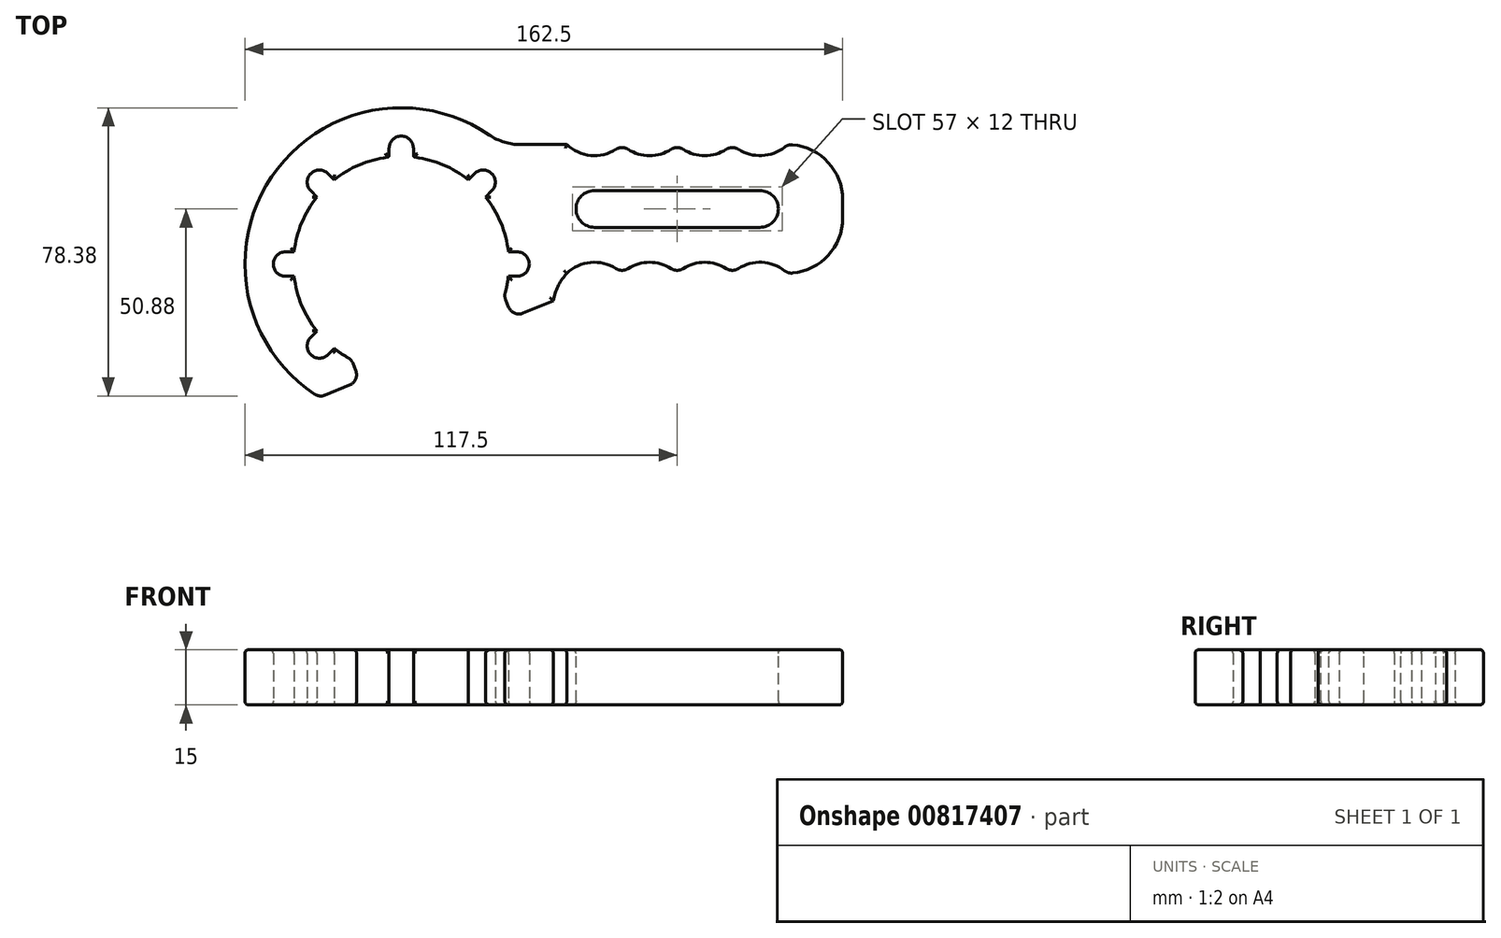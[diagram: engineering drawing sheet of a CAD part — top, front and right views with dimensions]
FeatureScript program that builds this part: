
annotation { "Feature Type Name" : "Feature", "Feature Type Description" : "" }
export const myFeature = defineFeature(function(context is Context, id is Id, definition is map)
    precondition{}
    {
        {
            var Q0;
            Q0=qCreatedBy(makeId("Top.planeOp"),FACE);
            var sketch = newSketch(context, id + "F0", { "sketchPlane" : qUnion([Q0])});
            skCircle(sketch, "E0", {"center": v(0, 0) * mm, "radius": 34.5 * mm});
            skLineSegment(sketch, "E1", {"start": v(0, 0) * mm, "end": v(0, 31.48) * mm, "construction": true});
            skLineSegment(sketch, "E2.bottom", {"start": v(-3.02, 0) * mm, "end": v(3.02, 0) * mm});
            skLineSegment(sketch, "E2.left", {"start": v(-3.02, 0) * mm, "end": v(-3.02, 34.37) * mm});
            skLineSegment(sketch, "E2.right", {"start": v(3.02, 0) * mm, "end": v(3.02, 34.37) * mm});
            skCircle(sketch, "E3", {"center": v(0, 0) * mm, "radius": 29 * mm});
            skCircle(sketch, "E4", {"center": v(0, 0) * mm, "radius": 12.5 * mm});
            skCircle(sketch, "E5", {"center": v(0, 31.48) * mm, "radius": 3.02 * mm});
            skPoint(sketch, "E5.first.point", {"position": v(0, 34.5) * mm});
            skPoint(sketch, "E5.second.point", {"position": v(-3.02, 31.48) * mm});
            skPoint(sketch, "E5.third.point", {"position": v(3.02, 31.48) * mm});
            skSolve(sketch);
        }
        {
            var Q0;
            {var subQ0=sQuery(id+"F0.wireOp",EDGE,"E5");var subQ2=sQuery(id+"F0.wireOp",EDGE,"E3");var subQ6=makeQuery(id+"F0.imprint","INTERSECT",VERTEX,{"disambiguationData":[OD(0.0)],"derivedFrom":[subQ2,subQ0]});Q0=makeQuery(id+"F0.imprint","IMPRINT",FACE,{"disambiguationData":[TD([[makeQuery(id+"F0.imprint","IMPRINT",EDGE,{"disambiguationData":[TD([[subQ6,-1.0]])],"derivedFrom":subQ2}),-1.0]])]});}
            var Q1;
            {var subQ0=sQuery(id+"F0.wireOp",EDGE,"E3");var subQ1=sQuery(id+"F0.wireOp",EDGE,"E2.left");var subQ2=makeQuery(id+"F0.imprint","INTERSECT",VERTEX,{"derivedFrom":[subQ1,subQ0]});Q1=makeQuery(id+"F0.imprint","IMPRINT",FACE,{"disambiguationData":[TD([[makeQuery(id+"F0.imprint","IMPRINT",EDGE,{"disambiguationData":[TD([[subQ2,-1.0]])],"derivedFrom":subQ1}),-1.0]])]});}
            var Q2;
            {var subQ0=sQuery(id+"F0.wireOp",EDGE,"E5");var subQ1=sQuery(id+"F0.wireOp",EDGE,"E3");var subQ2=makeQuery(id+"F0.imprint","INTERSECT",VERTEX,{"disambiguationData":[OD(0.0)],"derivedFrom":[subQ1,subQ0]});Q2=makeQuery(id+"F0.imprint","IMPRINT",FACE,{"disambiguationData":[TD([[makeQuery(id+"F0.imprint","IMPRINT",EDGE,{"disambiguationData":[TD([[subQ2,-1.0]])],"derivedFrom":subQ1}),1.0]])]});}
            var Q3;
            {var subQ0=sQuery(id+"F0.wireOp",EDGE,"E3");var subQ1=sQuery(id+"F0.wireOp",EDGE,"E2.right");var subQ2=makeQuery(id+"F0.imprint","INTERSECT",VERTEX,{"derivedFrom":[subQ1,subQ0]});Q3=makeQuery(id+"F0.imprint","IMPRINT",FACE,{"disambiguationData":[TD([[makeQuery(id+"F0.imprint","IMPRINT",EDGE,{"disambiguationData":[TD([[subQ2,-1.0]])],"derivedFrom":subQ1}),1.0]])]});}
            var Q4;
            {var subQ5=sQuery(id+"F0.wireOp",EDGE,"E2.left");var subQ8=sQuery(id+"F0.wireOp",EDGE,"E4");var subQ10=makeQuery(id+"F0.imprint","INTERSECT",VERTEX,{"derivedFrom":[subQ5,subQ8]});Q4=makeQuery(id+"F0.imprint","IMPRINT",FACE,{"disambiguationData":[TD([[makeQuery(id+"F0.imprint","IMPRINT",EDGE,{"disambiguationData":[TD([[subQ10,-1.0]])],"derivedFrom":subQ5}),-1.0]])]});}
            var Q5;
            {var subQ0=sQuery(id+"F0.wireOp",EDGE,"E2.bottom");Q5=makeQuery(id+"F0.imprint","IMPRINT",FACE,{"disambiguationData":[TD([[makeQuery(id+"F0.imprint","IMPRINT",EDGE,{"derivedFrom":subQ0}),-1.0]])]});}
            var Q6;
            {var subQ0=sQuery(id+"F0.wireOp",EDGE,"E2.bottom");Q6=makeQuery(id+"F0.imprint","IMPRINT",FACE,{"disambiguationData":[TD([[makeQuery(id+"F0.imprint","IMPRINT",EDGE,{"derivedFrom":subQ0}),1.0]])]});}
            var Q7;
            {var subQ0=sQuery(id+"F0.wireOp",EDGE,"E4");var subQ1=sQuery(id+"F0.wireOp",EDGE,"E2.left");var subQ2=makeQuery(id+"F0.imprint","INTERSECT",VERTEX,{"derivedFrom":[subQ1,subQ0]});Q7=makeQuery(id+"F0.imprint","IMPRINT",FACE,{"disambiguationData":[TD([[makeQuery(id+"F0.imprint","IMPRINT",EDGE,{"disambiguationData":[TD([[subQ2,-1.0]])],"derivedFrom":subQ1}),1.0]])]});}
            extrude(context, id + "F1", {"entities" : qUnion([Q0, Q1, Q2, Q3, Q4, Q5, Q6, Q7]), "depth" : 30 * mm, "offsetDistance" : 25 * mm});
        }
        {
            var Q0;
            Q0=makeQuery(id+"F1.opExtrude","SWEPT_BODY",BODY,{"disambiguationData":[OSD([sQuery(id+"F0.wireOp",EDGE,"E0"),sQuery(id+"F0.wireOp",EDGE,"E2.left"),sQuery(id+"F0.wireOp",EDGE,"E2.right"),sQuery(id+"F0.wireOp",EDGE,"E3"),sQuery(id+"F0.wireOp",EDGE,"E4")])]});
            var Q1;
            Q1=makeQuery(id+"F1.opExtrude","SWEPT_FACE",FACE,{"disambiguationData":[OSD([sQuery(id+"F0.wireOp",EDGE,"E3")])]});
            circularPattern(context, id + "F2", {"operationType" : NewBodyOperationType.ADD, "entities" : qUnion([Q0]), "axis" : qUnion([Q1]), "angle" : 360 * degree, "instanceCount" : 8, "equalSpace" : true});
        }
        {
            var Q0;
            {var subQ0=makeQuery(id+"F1.opExtrude","CAP_FACE",FACE,{"disambiguationData":[OSD([sQuery(id+"F0.wireOp",EDGE,"E0"),sQuery(id+"F0.wireOp",EDGE,"E2.left"),sQuery(id+"F0.wireOp",EDGE,"E2.right"),sQuery(id+"F0.wireOp",EDGE,"E3"),sQuery(id+"F0.wireOp",EDGE,"E4")])],"isStart":false});Q0=makeQuery(id+"F2.boolean.opBoolean","MERGE",FACE,{"derivedFrom":[subQ0,makeQuery(id+"F2.opPattern","COPY",FACE,{"derivedFrom":subQ0,"instanceName":"1"}),makeQuery(id+"F2.opPattern","COPY",FACE,{"derivedFrom":subQ0,"instanceName":"2"}),makeQuery(id+"F2.opPattern","COPY",FACE,{"derivedFrom":subQ0,"instanceName":"3"}),makeQuery(id+"F2.opPattern","COPY",FACE,{"derivedFrom":subQ0,"instanceName":"4"}),makeQuery(id+"F2.opPattern","COPY",FACE,{"derivedFrom":subQ0,"instanceName":"5"})]});}
            var sketch = newSketch(context, id + "F3", { "sketchPlane" : qUnion([Q0])});
            skCircle(sketch, "E6", {"center": v(0, 0) * mm, "radius": 42.5 * mm});
            skCircle(sketch, "E7", {"center": v(0, 0) * mm, "radius": 22.5 * mm});
            skLineSegment(sketch, "E8.bottom", {"start": v(0, 32.5) * mm, "end": v(120, 32.5) * mm});
            skLineSegment(sketch, "E8.top", {"start": v(0, -2.5) * mm, "end": v(120, -2.5) * mm});
            skLineSegment(sketch, "E8.left", {"start": v(0, 42.5) * mm, "end": v(0, -2.5) * mm});
            skLineSegment(sketch, "E8.right", {"start": v(120, 32.5) * mm, "end": v(120, -2.5) * mm});
            skLineSegment(sketch, "E9", {"start": v(0, 0) * mm, "end": v(25.3, -61.06) * mm, "construction": true});
            skLineSegment(sketch, "E10", {"start": v(20.79, 8.61) * mm, "end": v(46.08, -52.45) * mm});
            skLineSegment(sketch, "E11", {"start": v(46.08, -52.45) * mm, "end": v(4.5, -69.67) * mm});
            skLineSegment(sketch, "E12", {"start": v(4.5, -69.67) * mm, "end": v(-20.79, -8.61) * mm});
            skLineSegment(sketch, "E13", {"start": v(-20.79, -8.61) * mm, "end": v(20.79, 8.61) * mm});
            skLineSegment(sketch, "E14", {"start": v(-22.19, -36.25) * mm, "end": v(41.32, -9.94) * mm});
            skSolve(sketch);
        }
        {
            var Q0;
            {var subQ5=sQuery(id+"F3.wireOp",EDGE,"E8.right");Q0=makeQuery(id+"F3.imprint","IMPRINT",FACE,{"disambiguationData":[TD([[makeQuery(id+"F3.imprint","IMPRINT",EDGE,{"derivedFrom":subQ5}),-1.0]])]});}
            var Q1;
            {var subQ4=sQuery(id+"F0.wireOp",EDGE,"E2.right");var subQ5=makeQuery(id+"F1.opExtrude","CAP_EDGE",EDGE,{"disambiguationData":[OSD([subQ4])],"isStart":false});Q1=makeQuery(id+"F3.imprint","IMPRINT",FACE,{"disambiguationData":[TD([[makeQuery(id+"F3.imprint","IMPRINT",EDGE,{"derivedFrom":subQ5}),-1.0]])]});}
            var Q2;
            {var subQ3=sQuery(id+"F3.wireOp",EDGE,"E8.left");var subQ5=sQuery(id+"F3.wireOp",EDGE,"E6");var subQ6=makeQuery(id+"F3.imprint","INTERSECT",VERTEX,{"derivedFrom":[subQ5,subQ3]});Q2=makeQuery(id+"F3.imprint","IMPRINT",FACE,{"disambiguationData":[TD([[makeQuery(id+"F3.imprint","IMPRINT",EDGE,{"disambiguationData":[TD([[subQ6,1.0]])],"derivedFrom":subQ5}),1.0]])]});}
            var Q3;
            {var subQ2=sQuery(id+"F0.wireOp",EDGE,"E2.left");var subQ25=makeQuery(id+"F1.opExtrude","CAP_EDGE",EDGE,{"disambiguationData":[OSD([subQ2])],"isStart":false});Q3=makeQuery(id+"F3.imprint","IMPRINT",FACE,{"disambiguationData":[TD([[makeQuery(id+"F3.imprint","IMPRINT",EDGE,{"derivedFrom":subQ25}),1.0]])]});}
            var Q4;
            {var subQ5=sQuery(id+"F0.wireOp",EDGE,"E2.right");var subQ16=makeQuery(id+"F2.opPattern","COPY",EDGE,{"derivedFrom":makeQuery(id+"F1.opExtrude","CAP_EDGE",EDGE,{"disambiguationData":[OSD([subQ5])],"isStart":false}),"instanceName":"6"});Q4=makeQuery(id+"F3.imprint","IMPRINT",FACE,{"disambiguationData":[TD([[makeQuery(id+"F3.imprint","IMPRINT",EDGE,{"derivedFrom":subQ16}),-1.0]])]});}
            var Q5;
            {var subQ7=sQuery(id+"F0.wireOp",EDGE,"E2.right");var subQ8=makeQuery(id+"F2.opPattern","COPY",EDGE,{"derivedFrom":makeQuery(id+"F1.opExtrude","CAP_EDGE",EDGE,{"disambiguationData":[OSD([subQ7])],"isStart":false}),"instanceName":"2"});Q5=makeQuery(id+"F3.imprint","IMPRINT",FACE,{"disambiguationData":[TD([[makeQuery(id+"F3.imprint","IMPRINT",EDGE,{"derivedFrom":subQ8}),-1.0]])]});}
            var Q6;
            {var subQ0=makeQuery(id+"F1.opExtrude","CAP_FACE",FACE,{"disambiguationData":[OSD([sQuery(id+"F0.wireOp",EDGE,"E0"),sQuery(id+"F0.wireOp",EDGE,"E2.left"),sQuery(id+"F0.wireOp",EDGE,"E2.right"),sQuery(id+"F0.wireOp",EDGE,"E3"),sQuery(id+"F0.wireOp",EDGE,"E4")])],"isStart":false});Q6=makeQuery(id+"F2.boolean.opBoolean","MERGE",FACE,{"derivedFrom":[subQ0,makeQuery(id+"FdRA7V0R3QqqVRS_1.opRevolve","SWEPT_FACE",FACE,{"disambiguationData":[OSD([sQuery(id+"FKEeH5BDUjIDk6X_1.wireOp",EDGE,"wVb3vfNX-KfGu-E7eh-lrTJ-hg433LaZDyXz")])]}),makeQuery(id+"F2.opPattern","COPY",FACE,{"derivedFrom":subQ0,"instanceName":"1"}),makeQuery(id+"F2.opPattern","COPY",FACE,{"derivedFrom":subQ0,"instanceName":"2"}),makeQuery(id+"F2.opPattern","COPY",FACE,{"derivedFrom":subQ0,"instanceName":"3"}),makeQuery(id+"F2.opPattern","COPY",FACE,{"derivedFrom":subQ0,"instanceName":"4"}),makeQuery(id+"F2.opPattern","COPY",FACE,{"derivedFrom":subQ0,"instanceName":"5"})]});}
            extrude(context, id + "F4", {"entities" : qUnion([Q0, Q1, Q2, Q3, Q4, Q5]), "oppositeDirection" : true, "depth" : 15 * mm, "endBoundEntityFace" : qUnion([Q6]), "offsetDistance" : 25 * mm});
        }
        {
            var Q0;
            Q0=makeQuery(id+"F1.opExtrude","SWEPT_BODY",BODY,{"disambiguationData":[OSD([sQuery(id+"F0.wireOp",EDGE,"E0"),sQuery(id+"F0.wireOp",EDGE,"E2.left"),sQuery(id+"F0.wireOp",EDGE,"E2.right"),sQuery(id+"F0.wireOp",EDGE,"E3"),sQuery(id+"F0.wireOp",EDGE,"E4")])]});
            var Q1;
            Q1=makeQuery(id+"F4.opExtrude","SWEPT_BODY",BODY,{"disambiguationData":[OSD([sQuery(id+"F3.wireOp",EDGE,"E6")])]});
            booleanBodies(context, id + "F5", {"operationType" : BooleanOperationType.SUBTRACTION, "tools" : qUnion([Q0]), "targets" : qUnion([Q1]), "offset" : true, "offsetAll" : true, "offsetDistance" : .3 * mm});
        }
        {
            var Q0;
            Q0=makeQuery(id+"F4.opExtrude","CAP_FACE",FACE,{"disambiguationData":[OSD([sQuery(id+"F0.wireOp",EDGE,"E0"),sQuery(id+"F0.wireOp",EDGE,"E2.left"),sQuery(id+"F0.wireOp",EDGE,"E2.right"),sQuery(id+"F0.wireOp",EDGE,"E3"),sQuery(id+"F0.wireOp",EDGE,"68155f5a-aa5a-4abc-ae5a-2b9c3076ed17"),sQuery(id+"F0.wireOp",EDGE,"543f8d36-851c-4509-9e67-5f2352c07657"),sQuery(id+"F3.wireOp",EDGE,"E6"),sQuery(id+"F3.wireOp",EDGE,"E8.bottom"),sQuery(id+"F3.wireOp",EDGE,"E8.top"),sQuery(id+"F3.wireOp",EDGE,"E8.right"),sQuery(id+"F3.wireOp",EDGE,"E10"),sQuery(id+"F3.wireOp",EDGE,"E12"),sQuery(id+"F3.wireOp",EDGE,"E14")])],"isStart":true});
            var sketch = newSketch(context, id + "F6", { "sketchPlane" : qUnion([Q0])});
            skCircle(sketch, "E15", {"center": v(97.5, 40.37) * mm, "radius": 10.87 * mm});
            skCircle(sketch, "E16", {"center": v(97.5, -10.38) * mm, "radius": 10.87 * mm});
            skPoint(sketch, "E17", {"position": v(97.5, 29.5) * mm});
            skPoint(sketch, "E18", {"position": v(97.5, 0.5) * mm});
            skLineSegment(sketch, "E19", {"start": v(120, 15) * mm, "end": v(33.65, 15) * mm, "construction": true});
            skPoint(sketch, "E20", {"position": v(90, 32.5) * mm});
            skPoint(sketch, "E21", {"position": v(105, 32.5) * mm});
            skCircle(sketch, "E22.1.0.0", {"center": v(82.5, 40.37) * mm, "radius": 10.87 * mm});
            skCircle(sketch, "E22.1.0.1", {"center": v(82.5, -10.38) * mm, "radius": 10.87 * mm});
            skCircle(sketch, "E22.2.0.0", {"center": v(67.5, 40.37) * mm, "radius": 10.87 * mm});
            skCircle(sketch, "E22.2.0.1", {"center": v(67.5, -10.38) * mm, "radius": 10.87 * mm});
            skLineSegment(sketch, "E22.direction1", {"start": v(97.5, -10.38) * mm, "end": v(82.5, -10.38) * mm, "construction": true});
            skCircle(sketch, "E23.0.3.0", {"center": v(52.5, 40.37) * mm, "radius": 10.87 * mm});
            skCircle(sketch, "E23.2.3.0", {"center": v(52.5, -10.38) * mm, "radius": 10.87 * mm});
            skSolve(sketch);
        }
        {
            var Q0;
            Q0 = qSketchRegion(id + "F6", true);
            extrude(context, id + "F7", {"entities" : qUnion([Q0]), "operationType" : NewBodyOperationType.REMOVE, "endBound" : BoundingType.THROUGH_ALL, "oppositeDirection" : true, "depth" : 25 * mm, "offsetDistance" : 25 * mm});
        }
        {
            var Q0;
            Q0=makeQuery(id+"F4.opExtrude","CAP_FACE",FACE,{"disambiguationData":[OSD([sQuery(id+"F0.wireOp",EDGE,"E0"),sQuery(id+"F0.wireOp",EDGE,"E2.left"),sQuery(id+"F0.wireOp",EDGE,"E2.right"),sQuery(id+"F0.wireOp",EDGE,"E3"),sQuery(id+"F0.wireOp",EDGE,"68155f5a-aa5a-4abc-ae5a-2b9c3076ed17"),sQuery(id+"F0.wireOp",EDGE,"543f8d36-851c-4509-9e67-5f2352c07657"),sQuery(id+"F3.wireOp",EDGE,"E6"),sQuery(id+"F3.wireOp",EDGE,"E8.bottom"),sQuery(id+"F3.wireOp",EDGE,"E8.top"),sQuery(id+"F3.wireOp",EDGE,"E8.right"),sQuery(id+"F3.wireOp",EDGE,"E10"),sQuery(id+"F3.wireOp",EDGE,"E12"),sQuery(id+"F3.wireOp",EDGE,"E14")])],"isStart":true});
            var sketch = newSketch(context, id + "F8", { "sketchPlane" : qUnion([Q0])});
            skLineSegment(sketch, "E24.bottom", {"start": v(52.5, 20) * mm, "end": v(97.5, 20) * mm});
            skLineSegment(sketch, "E24.top", {"start": v(52.5, 10) * mm, "end": v(97.5, 10) * mm});
            skLineSegment(sketch, "E24.left", {"start": v(52.5, 20) * mm, "end": v(52.5, 10) * mm});
            skLineSegment(sketch, "E24.right", {"start": v(97.5, 20) * mm, "end": v(97.5, 10) * mm});
            skLineSegment(sketch, "E25", {"start": v(120, 15) * mm, "end": v(49.35, 15) * mm, "construction": true});
            skCircle(sketch, "E26", {"center": v(52.5, 15) * mm, "radius": 5 * mm});
            skCircle(sketch, "E27", {"center": v(97.5, 15) * mm, "radius": 5 * mm});
            skSolve(sketch);
        }
        {
            var Q0;
            Q0 = qSketchRegion(id + "F8", true);
            extrude(context, id + "F9", {"entities" : qUnion([Q0]), "operationType" : NewBodyOperationType.REMOVE, "endBound" : BoundingType.THROUGH_ALL, "oppositeDirection" : true, "depth" : 25 * mm, "offsetDistance" : 25 * mm});
        }
        {
            var Q0;
            Q0=makeQuery(id+"F4.opExtrude","SWEPT_EDGE",EDGE,{"disambiguationData":[OSD([sQuery(id+"F3.wireOp",EDGE,"E8.top"),sQuery(id+"F3.wireOp",EDGE,"E8.right")])]});
            var Q1;
            Q1=makeQuery(id+"F4.opExtrude","SWEPT_EDGE",EDGE,{"disambiguationData":[OSD([sQuery(id+"F3.wireOp",EDGE,"E6"),sQuery(id+"F3.wireOp",EDGE,"E8.bottom")])]});
            var Q2;
            Q2=makeQuery(id+"F4.opExtrude","SWEPT_EDGE",EDGE,{"disambiguationData":[OSD([sQuery(id+"F3.wireOp",EDGE,"E8.bottom"),sQuery(id+"F3.wireOp",EDGE,"E8.right")])]});
            var Q3;
            Q3=makeQuery(id+"F4.opExtrude","SWEPT_EDGE",EDGE,{"disambiguationData":[OSD([sQuery(id+"F3.wireOp",EDGE,"E6"),sQuery(id+"F3.wireOp",EDGE,"E8.top")])]});
            fillet(context, id + "F10", {"entities" : qUnion([Q0, Q1, Q2, Q3]), "radius" : 15 * mm, "tangentPropagation" : true, "allowEdgeOverflow" : false});
        }
        {
            var Q0;
            {var subQ1=sQuery(id+"F0.wireOp",EDGE,"E3");var subQ2=sQuery(id+"F0.wireOp",EDGE,"E2.right");Q0=makeQuery(id+"F5.tempBoolean.opBoolean","INTERSECT",EDGE,{"derivedFrom":[makeQuery(id+"F4.opExtrude","SWEPT_FACE",FACE,{"disambiguationData":[OSD([sQuery(id+"F3.wireOp",EDGE,"E10")])]}),makeQuery(id+"F5.offsetTempBody.opPattern","COPY",FACE,{"derivedFrom":makeQuery(id+"F2.boolean.opBoolean","SPLIT",FACE,{"disambiguationData":[TD([makeQuery(id+"F2.opPattern","COPY",FACE,{"derivedFrom":makeQuery(id+"F1.opExtrude","SWEPT_FACE",FACE,{"disambiguationData":[OSD([subQ2])]}),"instanceName":"2"})])],"derivedFrom":makeQuery(id+"F1.opExtrude","SWEPT_FACE",FACE,{"disambiguationData":[OSD([subQ1])]})}),"instanceName":"1"})]});}
            var Q1;
            {var subQ1=sQuery(id+"F0.wireOp",EDGE,"E3");var subQ2=sQuery(id+"F0.wireOp",EDGE,"E2.right");Q1=makeQuery(id+"F5.tempBoolean.opBoolean","INTERSECT",EDGE,{"derivedFrom":[makeQuery(id+"F4.opExtrude","SWEPT_FACE",FACE,{"disambiguationData":[OSD([sQuery(id+"F3.wireOp",EDGE,"E12")])]}),makeQuery(id+"F5.offsetTempBody.opPattern","COPY",FACE,{"derivedFrom":makeQuery(id+"F2.boolean.opBoolean","SPLIT",FACE,{"disambiguationData":[TD([makeQuery(id+"F2.opPattern","COPY",FACE,{"derivedFrom":makeQuery(id+"F1.opExtrude","SWEPT_FACE",FACE,{"disambiguationData":[OSD([subQ2])]}),"instanceName":"4"})])],"derivedFrom":makeQuery(id+"F1.opExtrude","SWEPT_FACE",FACE,{"disambiguationData":[OSD([subQ1])]})}),"instanceName":"1"})]});}
            var Q2;
            {var subQ0=sQuery(id+"F3.wireOp",EDGE,"E14");var subQ1=sQuery(id+"F3.wireOp",EDGE,"E6");Q2=makeQuery(id+"F4.opExtrude","SWEPT_EDGE",EDGE,{"disambiguationData":[OSD([subQ1,subQ0]),TDD([makeQuery(id+"F3.imprint","INTERSECT",VERTEX,{"disambiguationData":[OD(0.0)],"derivedFrom":[subQ1,subQ0]})])]});}
            var Q3;
            Q3=makeQuery(id+"F4.opExtrude","SWEPT_EDGE",EDGE,{"disambiguationData":[OSD([sQuery(id+"F3.wireOp",EDGE,"E12"),sQuery(id+"F3.wireOp",EDGE,"E14")])]});
            var Q4;
            Q4=makeQuery(id+"F4.opExtrude","SWEPT_EDGE",EDGE,{"disambiguationData":[OSD([sQuery(id+"F3.wireOp",EDGE,"E10"),sQuery(id+"F3.wireOp",EDGE,"E14")])]});
            var Q5;
            {var subQ0=sQuery(id+"F3.wireOp",EDGE,"E14");var subQ1=sQuery(id+"F3.wireOp",EDGE,"E6");Q5=makeQuery(id+"F10.opFillet","BLEND_EDGE",EDGE,{"blendedFrom":[makeQuery(id+"F4.opExtrude","SWEPT_EDGE",EDGE,{"disambiguationData":[OSD([subQ1,sQuery(id+"F3.wireOp",EDGE,"E8.top")])]}),makeQuery(id+"F4.opExtrude","SWEPT_FACE",FACE,{"disambiguationData":[OSD([subQ0]),TDD([makeQuery(id+"F3.imprint","IMPRINT",EDGE,{"disambiguationData":[TD([[makeQuery(id+"F3.imprint","INTERSECT",VERTEX,{"disambiguationData":[OD(1.0)],"derivedFrom":[subQ1,subQ0]}),1.0]])],"derivedFrom":subQ0})])]})],"blendedInto":[makeQuery(id+"F4.opExtrude","SWEPT_FACE",FACE,{"disambiguationData":[OSD([subQ0]),TDD([makeQuery(id+"F3.imprint","IMPRINT",EDGE,{"disambiguationData":[TD([[makeQuery(id+"F3.imprint","INTERSECT",VERTEX,{"disambiguationData":[OD(1.0)],"derivedFrom":[subQ1,subQ0]}),1.0]])],"derivedFrom":subQ0})])]})]});}
            var Q6;
            Q6=makeQuery(id+"F7.boolean.opBoolean","INTERSECT",EDGE,{"derivedFrom":[makeQuery(id+"F4.opExtrude","SWEPT_FACE",FACE,{"disambiguationData":[OSD([sQuery(id+"F3.wireOp",EDGE,"E8.top")])]}),makeQuery(id+"F7.opExtrude","SWEPT_FACE",FACE,{"disambiguationData":[OSD([sQuery(id+"F6.wireOp",EDGE,"c53bf962-9943-4c53-99a0-18143dd002e4.2.6.0")])]})]});
            var Q7;
            Q7=makeQuery(id+"F7.boolean.opBoolean","COPY",EDGE,{"derivedFrom":makeQuery(id+"F7.opExtrude","SWEPT_EDGE",EDGE,{"disambiguationData":[OSD([sQuery(id+"F3.wireOp",EDGE,"E8.top"),sQuery(id+"F6.wireOp",EDGE,"f3e3ac49-f856-4e77-8ba9-03a9cc5106c1.2.5.0"),sQuery(id+"F6.wireOp",EDGE,"c53bf962-9943-4c53-99a0-18143dd002e4.2.6.0")])]})});
            var Q8;
            Q8=makeQuery(id+"F7.boolean.opBoolean","COPY",EDGE,{"derivedFrom":makeQuery(id+"F7.opExtrude","SWEPT_EDGE",EDGE,{"disambiguationData":[OSD([sQuery(id+"F3.wireOp",EDGE,"E8.top"),sQuery(id+"F6.wireOp",EDGE,"9e121799-287f-4cef-9f42-af39a6b9019e.2.4.0"),sQuery(id+"F6.wireOp",EDGE,"f3e3ac49-f856-4e77-8ba9-03a9cc5106c1.2.5.0")])]})});
            var Q9;
            Q9=makeQuery(id+"F7.boolean.opBoolean","COPY",EDGE,{"derivedFrom":makeQuery(id+"F7.opExtrude","SWEPT_EDGE",EDGE,{"disambiguationData":[OSD([sQuery(id+"F3.wireOp",EDGE,"E8.top"),sQuery(id+"F6.wireOp",EDGE,"f8e0fc0a-a7f4-41af-85af-b59e38968203.2.3.0"),sQuery(id+"F6.wireOp",EDGE,"9e121799-287f-4cef-9f42-af39a6b9019e.2.4.0")])]})});
            var Q10;
            Q10=makeQuery(id+"F7.boolean.opBoolean","COPY",EDGE,{"derivedFrom":makeQuery(id+"F7.opExtrude","SWEPT_EDGE",EDGE,{"disambiguationData":[OSD([sQuery(id+"F3.wireOp",EDGE,"E8.top"),sQuery(id+"F6.wireOp",EDGE,"E22.2.0.1"),sQuery(id+"F6.wireOp",EDGE,"f8e0fc0a-a7f4-41af-85af-b59e38968203.2.3.0")])]})});
            var Q11;
            Q11=makeQuery(id+"F7.boolean.opBoolean","COPY",EDGE,{"derivedFrom":makeQuery(id+"F7.opExtrude","SWEPT_EDGE",EDGE,{"disambiguationData":[OSD([sQuery(id+"F3.wireOp",EDGE,"E8.top"),sQuery(id+"F6.wireOp",EDGE,"E22.1.0.1"),sQuery(id+"F6.wireOp",EDGE,"E22.2.0.1")])]})});
            var Q12;
            Q12=makeQuery(id+"F7.boolean.opBoolean","COPY",EDGE,{"derivedFrom":makeQuery(id+"F7.opExtrude","SWEPT_EDGE",EDGE,{"disambiguationData":[OSD([sQuery(id+"F3.wireOp",EDGE,"E8.top"),sQuery(id+"F6.wireOp",EDGE,"E16"),sQuery(id+"F6.wireOp",EDGE,"E22.1.0.1")])]})});
            var Q13;
            Q13=makeQuery(id+"F10.opFillet","BLEND_EDGE",EDGE,{"blendedFrom":[makeQuery(id+"F4.opExtrude","SWEPT_EDGE",EDGE,{"disambiguationData":[OSD([sQuery(id+"F3.wireOp",EDGE,"E8.top"),sQuery(id+"F3.wireOp",EDGE,"E8.right")])]}),makeQuery(id+"F7.boolean.opBoolean","COPY",FACE,{"derivedFrom":makeQuery(id+"F7.opExtrude","SWEPT_FACE",FACE,{"disambiguationData":[OSD([sQuery(id+"F6.wireOp",EDGE,"E16")])]})})],"blendedInto":[makeQuery(id+"F7.boolean.opBoolean","COPY",FACE,{"derivedFrom":makeQuery(id+"F7.opExtrude","SWEPT_FACE",FACE,{"disambiguationData":[OSD([sQuery(id+"F6.wireOp",EDGE,"E16")])]})})]});
            var Q14;
            Q14=makeQuery(id+"F10.opFillet","BLEND_EDGE",EDGE,{"blendedFrom":[makeQuery(id+"F4.opExtrude","SWEPT_EDGE",EDGE,{"disambiguationData":[OSD([sQuery(id+"F3.wireOp",EDGE,"E8.bottom"),sQuery(id+"F3.wireOp",EDGE,"E8.right")])]}),makeQuery(id+"F7.boolean.opBoolean","COPY",FACE,{"derivedFrom":makeQuery(id+"F7.opExtrude","SWEPT_FACE",FACE,{"disambiguationData":[OSD([sQuery(id+"F6.wireOp",EDGE,"E15")])]})})],"blendedInto":[makeQuery(id+"F7.boolean.opBoolean","COPY",FACE,{"derivedFrom":makeQuery(id+"F7.opExtrude","SWEPT_FACE",FACE,{"disambiguationData":[OSD([sQuery(id+"F6.wireOp",EDGE,"E15")])]})})]});
            var Q15;
            Q15=makeQuery(id+"F7.boolean.opBoolean","COPY",EDGE,{"derivedFrom":makeQuery(id+"F7.opExtrude","SWEPT_EDGE",EDGE,{"disambiguationData":[OSD([sQuery(id+"F3.wireOp",EDGE,"E8.bottom"),sQuery(id+"F6.wireOp",EDGE,"E15"),sQuery(id+"F6.wireOp",EDGE,"E22.1.0.0")])]})});
            var Q16;
            Q16=makeQuery(id+"F7.boolean.opBoolean","COPY",EDGE,{"derivedFrom":makeQuery(id+"F7.opExtrude","SWEPT_EDGE",EDGE,{"disambiguationData":[OSD([sQuery(id+"F3.wireOp",EDGE,"E8.bottom"),sQuery(id+"F6.wireOp",EDGE,"E22.1.0.0"),sQuery(id+"F6.wireOp",EDGE,"E22.2.0.0")])]})});
            var Q17;
            Q17=makeQuery(id+"F7.boolean.opBoolean","COPY",EDGE,{"derivedFrom":makeQuery(id+"F7.opExtrude","SWEPT_EDGE",EDGE,{"disambiguationData":[OSD([sQuery(id+"F3.wireOp",EDGE,"E8.bottom"),sQuery(id+"F6.wireOp",EDGE,"E22.2.0.0"),sQuery(id+"F6.wireOp",EDGE,"f8e0fc0a-a7f4-41af-85af-b59e38968203.0.3.0")])]})});
            var Q18;
            Q18=makeQuery(id+"F7.boolean.opBoolean","COPY",EDGE,{"derivedFrom":makeQuery(id+"F7.opExtrude","SWEPT_EDGE",EDGE,{"disambiguationData":[OSD([sQuery(id+"F3.wireOp",EDGE,"E8.bottom"),sQuery(id+"F6.wireOp",EDGE,"f8e0fc0a-a7f4-41af-85af-b59e38968203.0.3.0"),sQuery(id+"F6.wireOp",EDGE,"9e121799-287f-4cef-9f42-af39a6b9019e.0.4.0")])]})});
            var Q19;
            Q19=makeQuery(id+"F7.boolean.opBoolean","COPY",EDGE,{"derivedFrom":makeQuery(id+"F7.opExtrude","SWEPT_EDGE",EDGE,{"disambiguationData":[OSD([sQuery(id+"F3.wireOp",EDGE,"E8.bottom"),sQuery(id+"F6.wireOp",EDGE,"9e121799-287f-4cef-9f42-af39a6b9019e.0.4.0"),sQuery(id+"F6.wireOp",EDGE,"f3e3ac49-f856-4e77-8ba9-03a9cc5106c1.0.5.0")])]})});
            var Q20;
            Q20=makeQuery(id+"F7.boolean.opBoolean","COPY",EDGE,{"derivedFrom":makeQuery(id+"F7.opExtrude","SWEPT_EDGE",EDGE,{"disambiguationData":[OSD([sQuery(id+"F3.wireOp",EDGE,"E8.bottom"),sQuery(id+"F6.wireOp",EDGE,"f3e3ac49-f856-4e77-8ba9-03a9cc5106c1.0.5.0"),sQuery(id+"F6.wireOp",EDGE,"c53bf962-9943-4c53-99a0-18143dd002e4.0.6.0")])]})});
            var Q21;
            Q21=makeQuery(id+"F7.boolean.opBoolean","INTERSECT",EDGE,{"derivedFrom":[makeQuery(id+"F4.opExtrude","SWEPT_FACE",FACE,{"disambiguationData":[OSD([sQuery(id+"F3.wireOp",EDGE,"E8.bottom")])]}),makeQuery(id+"F7.opExtrude","SWEPT_FACE",FACE,{"disambiguationData":[OSD([sQuery(id+"F6.wireOp",EDGE,"c53bf962-9943-4c53-99a0-18143dd002e4.0.6.0")])]})]});
            fillet(context, id + "F11", {"entities" : qUnion([Q0, Q1, Q2, Q3, Q4, Q5, Q6, Q7, Q8, Q9, Q10, Q11, Q12, Q13, Q14, Q15, Q16, Q17, Q18, Q19, Q20, Q21]), "radius" : 3 * mm, "tangentPropagation" : true, "allowEdgeOverflow" : false});
        }
        {
            var Q0;
            Q0=makeQuery(id+"F5.tempBoolean.opBoolean","COPY",EDGE,{"derivedFrom":makeQuery(id+"F5.offsetTempBody.opPattern","COPY",EDGE,{"derivedFrom":makeQuery(id+"F2.opPattern","COPY",EDGE,{"derivedFrom":makeQuery(id+"F1.opExtrude","SWEPT_EDGE",EDGE,{"disambiguationData":[OSD([sQuery(id+"F0.wireOp",EDGE,"E2.right"),sQuery(id+"F0.wireOp",EDGE,"E3")])]}),"instanceName":"1"}),"instanceName":"1"})});
            var Q1;
            Q1=makeQuery(id+"F5.tempBoolean.opBoolean","COPY",EDGE,{"derivedFrom":makeQuery(id+"F5.offsetTempBody.opPattern","COPY",EDGE,{"derivedFrom":makeQuery(id+"F2.opPattern","COPY",EDGE,{"derivedFrom":makeQuery(id+"F1.opExtrude","SWEPT_EDGE",EDGE,{"disambiguationData":[OSD([sQuery(id+"F0.wireOp",EDGE,"E2.left"),sQuery(id+"F0.wireOp",EDGE,"E3")])]}),"instanceName":"1"}),"instanceName":"1"})});
            var Q2;
            {var subQ0=makeQuery(id+"F1.opExtrude","SWEPT_FACE",FACE,{"disambiguationData":[OSD([sQuery(id+"F0.wireOp",EDGE,"E3")])]});Q2=makeQuery(id+"F5.tempBoolean.opBoolean","COPY",EDGE,{"derivedFrom":makeQuery(id+"F5.offsetTempBody.opPattern","COPY",EDGE,{"derivedFrom":makeQuery(id+"F2.boolean.opBoolean","INTERSECT",EDGE,{"disambiguationData":[topologyDisambiguationEdgeConnected([makeQuery(id+"F2.opPattern","COPY",FACE,{"derivedFrom":makeQuery(id+"F1.opExtrude","SWEPT_FACE",FACE,{"disambiguationData":[OSD([sQuery(id+"F0.wireOp",EDGE,"E2.right")])]}),"instanceName":"2"})])],"derivedFrom":[makeQuery(id+"F2.opPattern","COPY",FACE,{"derivedFrom":subQ0,"instanceName":"1"}),makeQuery(id+"F2.opPattern","COPY",FACE,{"derivedFrom":subQ0,"instanceName":"3"})]}),"instanceName":"1"})});}
            var Q3;
            {var subQ0=makeQuery(id+"F1.opExtrude","SWEPT_FACE",FACE,{"disambiguationData":[OSD([sQuery(id+"F0.wireOp",EDGE,"E3")])]});Q3=makeQuery(id+"F5.tempBoolean.opBoolean","COPY",EDGE,{"derivedFrom":makeQuery(id+"F5.offsetTempBody.opPattern","COPY",EDGE,{"derivedFrom":makeQuery(id+"F2.boolean.opBoolean","INTERSECT",EDGE,{"disambiguationData":[topologyDisambiguationEdgeConnected([makeQuery(id+"F2.opPattern","COPY",FACE,{"derivedFrom":makeQuery(id+"F1.opExtrude","SWEPT_FACE",FACE,{"disambiguationData":[OSD([sQuery(id+"F0.wireOp",EDGE,"E2.left")])]}),"instanceName":"2"})])],"derivedFrom":[makeQuery(id+"F2.opPattern","COPY",FACE,{"derivedFrom":subQ0,"instanceName":"1"}),makeQuery(id+"F2.opPattern","COPY",FACE,{"derivedFrom":subQ0,"instanceName":"3"})]}),"instanceName":"1"})});}
            var Q4;
            {var subQ0=makeQuery(id+"F1.opExtrude","SWEPT_FACE",FACE,{"disambiguationData":[OSD([sQuery(id+"F0.wireOp",EDGE,"E3")])]});Q4=makeQuery(id+"F5.tempBoolean.opBoolean","COPY",EDGE,{"derivedFrom":makeQuery(id+"F5.offsetTempBody.opPattern","COPY",EDGE,{"derivedFrom":makeQuery(id+"F2.boolean.opBoolean","INTERSECT",EDGE,{"disambiguationData":[topologyDisambiguationEdgeConnected([makeQuery(id+"F2.opPattern","COPY",FACE,{"derivedFrom":makeQuery(id+"F1.opExtrude","SWEPT_FACE",FACE,{"disambiguationData":[OSD([sQuery(id+"F0.wireOp",EDGE,"E2.right")])]}),"instanceName":"3"})])],"derivedFrom":[makeQuery(id+"F2.opPattern","COPY",FACE,{"derivedFrom":subQ0,"instanceName":"1"}),makeQuery(id+"F2.opPattern","COPY",FACE,{"derivedFrom":subQ0,"instanceName":"2"}),makeQuery(id+"F2.opPattern","COPY",FACE,{"derivedFrom":subQ0,"instanceName":"4"})]}),"instanceName":"1"})});}
            var Q5;
            Q5=makeQuery(id+"F5.tempBoolean.opBoolean","COPY",EDGE,{"derivedFrom":makeQuery(id+"F5.offsetTempBody.opPattern","COPY",EDGE,{"derivedFrom":makeQuery(id+"F1.opExtrude","SWEPT_EDGE",EDGE,{"disambiguationData":[OSD([sQuery(id+"F0.wireOp",EDGE,"E2.left"),sQuery(id+"F0.wireOp",EDGE,"E3")])]}),"instanceName":"1"})});
            var Q6;
            Q6=makeQuery(id+"F5.tempBoolean.opBoolean","COPY",EDGE,{"derivedFrom":makeQuery(id+"F5.offsetTempBody.opPattern","COPY",EDGE,{"derivedFrom":makeQuery(id+"F1.opExtrude","SWEPT_EDGE",EDGE,{"disambiguationData":[OSD([sQuery(id+"F0.wireOp",EDGE,"E2.right"),sQuery(id+"F0.wireOp",EDGE,"E3")])]}),"instanceName":"1"})});
            var Q7;
            {var subQ0=makeQuery(id+"F1.opExtrude","SWEPT_FACE",FACE,{"disambiguationData":[OSD([sQuery(id+"F0.wireOp",EDGE,"E3")])]});Q7=makeQuery(id+"F5.tempBoolean.opBoolean","COPY",EDGE,{"derivedFrom":makeQuery(id+"F5.offsetTempBody.opPattern","COPY",EDGE,{"derivedFrom":makeQuery(id+"F2.boolean.opBoolean","INTERSECT",EDGE,{"disambiguationData":[topologyDisambiguationEdgeConnected([makeQuery(id+"F2.opPattern","COPY",FACE,{"derivedFrom":makeQuery(id+"F1.opExtrude","SWEPT_FACE",FACE,{"disambiguationData":[OSD([sQuery(id+"F0.wireOp",EDGE,"E2.left")])]}),"instanceName":"7"})])],"derivedFrom":[makeQuery(id+"F2.opPattern","COPY",FACE,{"derivedFrom":subQ0,"instanceName":"1"}),makeQuery(id+"F2.opPattern","COPY",FACE,{"derivedFrom":subQ0,"instanceName":"2"}),makeQuery(id+"F2.opPattern","COPY",FACE,{"derivedFrom":subQ0,"instanceName":"3"}),makeQuery(id+"F2.opPattern","COPY",FACE,{"derivedFrom":subQ0,"instanceName":"4"}),makeQuery(id+"F2.opPattern","COPY",FACE,{"derivedFrom":subQ0,"instanceName":"5"}),makeQuery(id+"F2.opPattern","COPY",FACE,{"derivedFrom":subQ0,"instanceName":"6"})]}),"instanceName":"1"})});}
            var Q8;
            {var subQ0=makeQuery(id+"F1.opExtrude","SWEPT_FACE",FACE,{"disambiguationData":[OSD([sQuery(id+"F0.wireOp",EDGE,"E3")])]});Q8=makeQuery(id+"F5.tempBoolean.opBoolean","COPY",EDGE,{"derivedFrom":makeQuery(id+"F5.offsetTempBody.opPattern","COPY",EDGE,{"derivedFrom":makeQuery(id+"F2.boolean.opBoolean","INTERSECT",EDGE,{"disambiguationData":[topologyDisambiguationEdgeConnected([makeQuery(id+"F2.opPattern","COPY",FACE,{"derivedFrom":makeQuery(id+"F1.opExtrude","SWEPT_FACE",FACE,{"disambiguationData":[OSD([sQuery(id+"F0.wireOp",EDGE,"E2.right")])]}),"instanceName":"7"})])],"derivedFrom":[makeQuery(id+"F2.opPattern","COPY",FACE,{"derivedFrom":subQ0,"instanceName":"1"}),makeQuery(id+"F2.opPattern","COPY",FACE,{"derivedFrom":subQ0,"instanceName":"2"}),makeQuery(id+"F2.opPattern","COPY",FACE,{"derivedFrom":subQ0,"instanceName":"3"}),makeQuery(id+"F2.opPattern","COPY",FACE,{"derivedFrom":subQ0,"instanceName":"4"}),makeQuery(id+"F2.opPattern","COPY",FACE,{"derivedFrom":subQ0,"instanceName":"5"}),makeQuery(id+"F2.opPattern","COPY",FACE,{"derivedFrom":subQ0,"instanceName":"6"})]}),"instanceName":"1"})});}
            var Q9;
            {var subQ0=makeQuery(id+"F1.opExtrude","SWEPT_FACE",FACE,{"disambiguationData":[OSD([sQuery(id+"F0.wireOp",EDGE,"E3")])]});Q9=makeQuery(id+"F5.tempBoolean.opBoolean","COPY",EDGE,{"derivedFrom":makeQuery(id+"F5.offsetTempBody.opPattern","COPY",EDGE,{"derivedFrom":makeQuery(id+"F2.boolean.opBoolean","INTERSECT",EDGE,{"disambiguationData":[topologyDisambiguationEdgeConnected([makeQuery(id+"F2.opPattern","COPY",FACE,{"derivedFrom":makeQuery(id+"F1.opExtrude","SWEPT_FACE",FACE,{"disambiguationData":[OSD([sQuery(id+"F0.wireOp",EDGE,"E2.left")])]}),"instanceName":"6"})])],"derivedFrom":[makeQuery(id+"F2.opPattern","COPY",FACE,{"derivedFrom":subQ0,"instanceName":"1"}),makeQuery(id+"F2.opPattern","COPY",FACE,{"derivedFrom":subQ0,"instanceName":"2"}),makeQuery(id+"F2.opPattern","COPY",FACE,{"derivedFrom":subQ0,"instanceName":"3"}),makeQuery(id+"F2.opPattern","COPY",FACE,{"derivedFrom":subQ0,"instanceName":"4"}),makeQuery(id+"F2.opPattern","COPY",FACE,{"derivedFrom":subQ0,"instanceName":"5"}),makeQuery(id+"F2.opPattern","COPY",FACE,{"derivedFrom":subQ0,"instanceName":"7"})]}),"instanceName":"1"})});}
            var Q10;
            {var subQ0=makeQuery(id+"F1.opExtrude","SWEPT_FACE",FACE,{"disambiguationData":[OSD([sQuery(id+"F0.wireOp",EDGE,"E3")])]});Q10=makeQuery(id+"F5.tempBoolean.opBoolean","COPY",EDGE,{"derivedFrom":makeQuery(id+"F5.offsetTempBody.opPattern","COPY",EDGE,{"derivedFrom":makeQuery(id+"F2.boolean.opBoolean","INTERSECT",EDGE,{"disambiguationData":[topologyDisambiguationEdgeConnected([makeQuery(id+"F2.opPattern","COPY",FACE,{"derivedFrom":makeQuery(id+"F1.opExtrude","SWEPT_FACE",FACE,{"disambiguationData":[OSD([sQuery(id+"F0.wireOp",EDGE,"E2.left")])]}),"instanceName":"3"})])],"derivedFrom":[makeQuery(id+"F2.opPattern","COPY",FACE,{"derivedFrom":subQ0,"instanceName":"1"}),makeQuery(id+"F2.opPattern","COPY",FACE,{"derivedFrom":subQ0,"instanceName":"2"}),makeQuery(id+"F2.opPattern","COPY",FACE,{"derivedFrom":subQ0,"instanceName":"4"})]}),"instanceName":"1"})});}
            var Q11;
            {var subQ0=makeQuery(id+"F1.opExtrude","SWEPT_FACE",FACE,{"disambiguationData":[OSD([sQuery(id+"F0.wireOp",EDGE,"E3")])]});Q11=makeQuery(id+"F5.tempBoolean.opBoolean","COPY",EDGE,{"derivedFrom":makeQuery(id+"F5.offsetTempBody.opPattern","COPY",EDGE,{"derivedFrom":makeQuery(id+"F2.boolean.opBoolean","INTERSECT",EDGE,{"disambiguationData":[topologyDisambiguationEdgeConnected([makeQuery(id+"F2.opPattern","COPY",FACE,{"derivedFrom":makeQuery(id+"F1.opExtrude","SWEPT_FACE",FACE,{"disambiguationData":[OSD([sQuery(id+"F0.wireOp",EDGE,"E2.right")])]}),"instanceName":"6"})])],"derivedFrom":[makeQuery(id+"F2.opPattern","COPY",FACE,{"derivedFrom":subQ0,"instanceName":"1"}),makeQuery(id+"F2.opPattern","COPY",FACE,{"derivedFrom":subQ0,"instanceName":"2"}),makeQuery(id+"F2.opPattern","COPY",FACE,{"derivedFrom":subQ0,"instanceName":"3"}),makeQuery(id+"F2.opPattern","COPY",FACE,{"derivedFrom":subQ0,"instanceName":"4"}),makeQuery(id+"F2.opPattern","COPY",FACE,{"derivedFrom":subQ0,"instanceName":"5"}),makeQuery(id+"F2.opPattern","COPY",FACE,{"derivedFrom":subQ0,"instanceName":"7"})]}),"instanceName":"1"})});}
            var Q12;
            {var subQ0=makeQuery(id+"F1.opExtrude","SWEPT_FACE",FACE,{"disambiguationData":[OSD([sQuery(id+"F0.wireOp",EDGE,"E3")])]});Q12=makeQuery(id+"F5.tempBoolean.opBoolean","COPY",EDGE,{"derivedFrom":makeQuery(id+"F5.offsetTempBody.opPattern","COPY",EDGE,{"derivedFrom":makeQuery(id+"F2.boolean.opBoolean","INTERSECT",EDGE,{"disambiguationData":[topologyDisambiguationEdgeConnected([makeQuery(id+"F2.opPattern","COPY",FACE,{"derivedFrom":makeQuery(id+"F1.opExtrude","SWEPT_FACE",FACE,{"disambiguationData":[OSD([sQuery(id+"F0.wireOp",EDGE,"E2.left")])]}),"instanceName":"5"})])],"derivedFrom":[makeQuery(id+"F2.opPattern","COPY",FACE,{"derivedFrom":subQ0,"instanceName":"1"}),makeQuery(id+"F2.opPattern","COPY",FACE,{"derivedFrom":subQ0,"instanceName":"2"}),makeQuery(id+"F2.opPattern","COPY",FACE,{"derivedFrom":subQ0,"instanceName":"3"}),makeQuery(id+"F2.opPattern","COPY",FACE,{"derivedFrom":subQ0,"instanceName":"4"}),makeQuery(id+"F2.opPattern","COPY",FACE,{"derivedFrom":subQ0,"instanceName":"6"})]}),"instanceName":"1"})});}
            var Q13;
            {var subQ0=makeQuery(id+"F1.opExtrude","SWEPT_FACE",FACE,{"disambiguationData":[OSD([sQuery(id+"F0.wireOp",EDGE,"E3")])]});Q13=makeQuery(id+"F5.tempBoolean.opBoolean","COPY",EDGE,{"derivedFrom":makeQuery(id+"F5.offsetTempBody.opPattern","COPY",EDGE,{"derivedFrom":makeQuery(id+"F2.boolean.opBoolean","INTERSECT",EDGE,{"disambiguationData":[topologyDisambiguationEdgeConnected([makeQuery(id+"F2.opPattern","COPY",FACE,{"derivedFrom":makeQuery(id+"F1.opExtrude","SWEPT_FACE",FACE,{"disambiguationData":[OSD([sQuery(id+"F0.wireOp",EDGE,"E2.right")])]}),"instanceName":"5"})])],"derivedFrom":[makeQuery(id+"F2.opPattern","COPY",FACE,{"derivedFrom":subQ0,"instanceName":"1"}),makeQuery(id+"F2.opPattern","COPY",FACE,{"derivedFrom":subQ0,"instanceName":"2"}),makeQuery(id+"F2.opPattern","COPY",FACE,{"derivedFrom":subQ0,"instanceName":"3"}),makeQuery(id+"F2.opPattern","COPY",FACE,{"derivedFrom":subQ0,"instanceName":"4"}),makeQuery(id+"F2.opPattern","COPY",FACE,{"derivedFrom":subQ0,"instanceName":"6"})]}),"instanceName":"1"})});}
            fillet(context, id + "F12", {"entities" : qUnion([Q0, Q1, Q2, Q3, Q4, Q5, Q6, Q7, Q8, Q9, Q10, Q11, Q12, Q13]), "radius" : .5 * mm, "tangentPropagation" : true, "allowEdgeOverflow" : false});
        }
        {
            var Q0;
            Q0=makeQuery(id+"F4.opExtrude","CAP_FACE",FACE,{"disambiguationData":[OSD([sQuery(id+"F3.wireOp",EDGE,"E6"),sQuery(id+"F3.wireOp",EDGE,"E7"),sQuery(id+"F3.wireOp",EDGE,"E8.bottom"),sQuery(id+"F3.wireOp",EDGE,"E8.top"),sQuery(id+"F3.wireOp",EDGE,"E8.right")])],"isStart":true});
            var Q1;
            Q1=makeQuery(id+"F4.opExtrude","CAP_FACE",FACE,{"disambiguationData":[OSD([sQuery(id+"F3.wireOp",EDGE,"E6"),sQuery(id+"F3.wireOp",EDGE,"E7"),sQuery(id+"F3.wireOp",EDGE,"E8.bottom"),sQuery(id+"F3.wireOp",EDGE,"E8.top"),sQuery(id+"F3.wireOp",EDGE,"E8.right")])],"isStart":false});
            fillet(context, id + "F13", {"entities" : qUnion([Q0, Q1]), "radius" : 1 * mm, "tangentPropagation" : true, "allowEdgeOverflow" : false});
        }
    });
